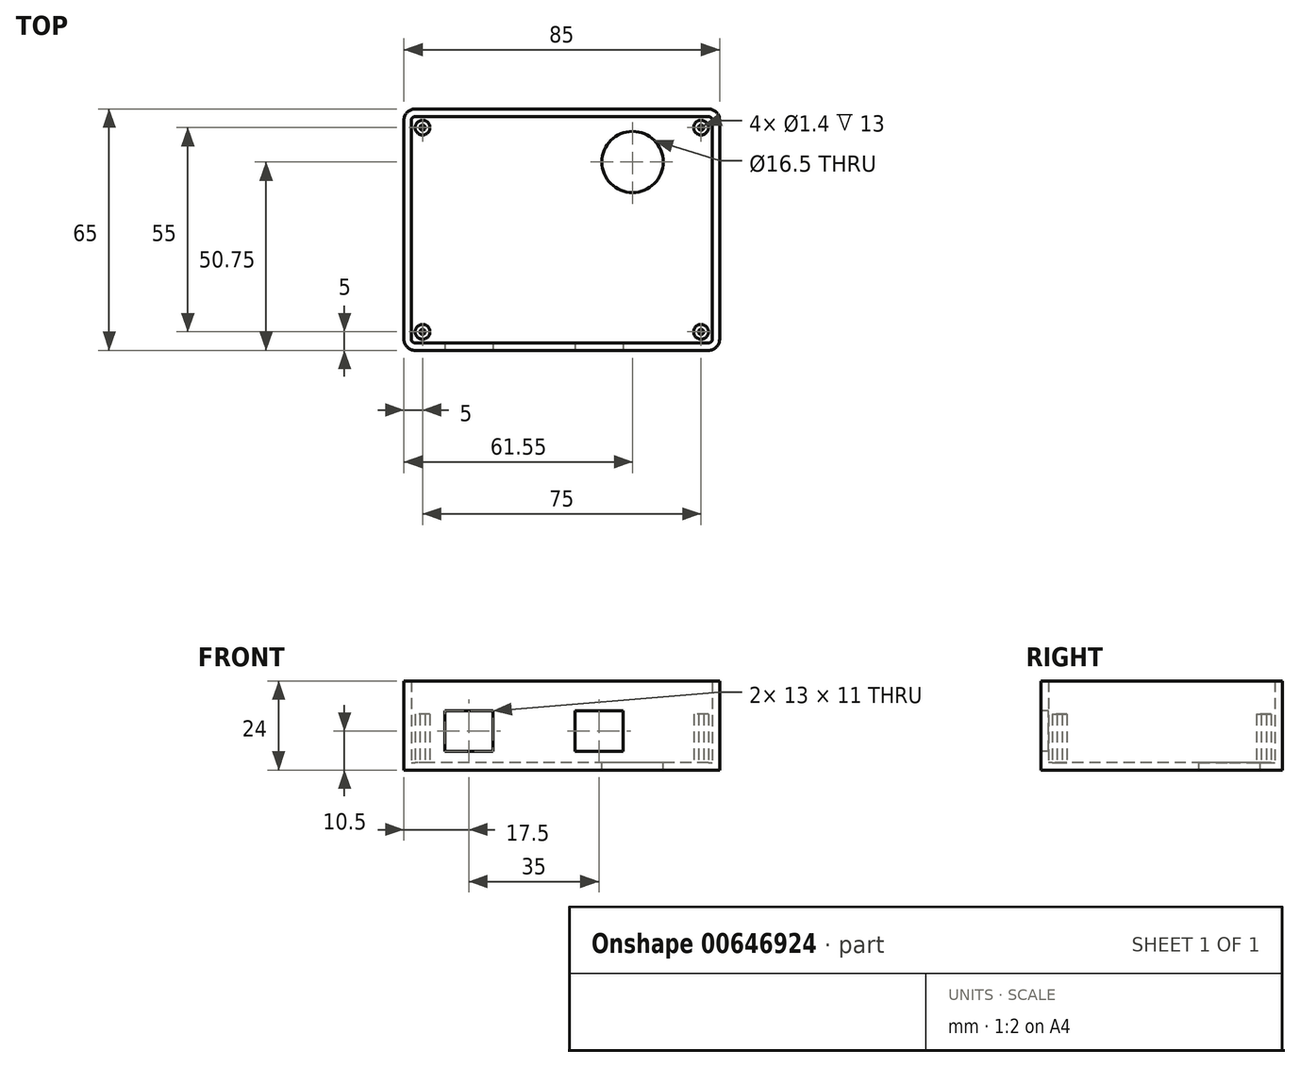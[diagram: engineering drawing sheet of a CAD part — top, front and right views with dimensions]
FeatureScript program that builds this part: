
annotation { "Feature Type Name" : "Feature", "Feature Type Description" : "" }
export const myFeature = defineFeature(function(context is Context, id is Id, definition is map)
    precondition{}
    {
        {
            var Q0;
            Q0=qCreatedBy(makeId("Top.planeOp"),FACE);
            var sketch = newSketch(context, id + "F0", { "sketchPlane" : qUnion([Q0])});
            skLineSegment(sketch, "E0.bottom", {"start": v(39.5, 32.5) * mm, "end": v(-39.5, 32.5) * mm});
            skLineSegment(sketch, "E0.top", {"start": v(39.5, -32.5) * mm, "end": v(-39.5, -32.5) * mm});
            skLineSegment(sketch, "E0.left", {"start": v(42.5, 29.5) * mm, "end": v(42.5, -29.5) * mm});
            skLineSegment(sketch, "E0.right", {"start": v(-42.5, 29.5) * mm, "end": v(-42.5, -29.5) * mm});
            skPoint(sketch, "E0.middle", {"position": v(0, 0) * mm});
            skPoint(sketch, "E1.visualSharp", {"position": v(-42.5, 32.5) * mm});
            skArc(sketch, "E1.filletArc", {"start": v(-39.5, 32.5) * mm, "mid": v(-41.62, 31.62) * mm, "end": v(-42.5, 29.5) * mm});
            skPoint(sketch, "E2.visualSharp", {"position": v(-42.5, -32.5) * mm});
            skArc(sketch, "E2.filletArc", {"start": v(-42.5, -29.5) * mm, "mid": v(-41.62, -31.62) * mm, "end": v(-39.5, -32.5) * mm});
            skPoint(sketch, "E3.visualSharp", {"position": v(42.5, -32.5) * mm});
            skArc(sketch, "E3.filletArc", {"start": v(39.5, -32.5) * mm, "mid": v(41.62, -31.62) * mm, "end": v(42.5, -29.5) * mm});
            skPoint(sketch, "E4.visualSharp", {"position": v(42.5, 32.5) * mm});
            skArc(sketch, "E4.filletArc", {"start": v(42.5, 29.5) * mm, "mid": v(41.62, 31.62) * mm, "end": v(39.5, 32.5) * mm});
            skSolve(sketch);
        }
        {
            var Q0;
            Q0=makeQuery(id+"F0.imprint","IMPRINT",FACE,{"disambiguationData":[TD([[makeQuery(id+"F0.imprint","IMPRINT",EDGE,{"derivedFrom":sQuery(id+"F0.wireOp",EDGE,"E0.bottom")}),1.0]])]});
            extrude(context, id + "F1", {"entities" : qUnion([Q0]), "depth" : 24 * mm, "offsetDistance" : 25 * mm});
        }
        {
            var Q0;
            Q0=makeQuery(id+"F1.opExtrude","CAP_FACE",FACE,{"disambiguationData":[OSD([sQuery(id+"F0.wireOp",EDGE,"E0.bottom"),sQuery(id+"F0.wireOp",EDGE,"E0.top"),sQuery(id+"F0.wireOp",EDGE,"E0.left"),sQuery(id+"F0.wireOp",EDGE,"E0.right"),sQuery(id+"F0.wireOp",EDGE,"E1.filletArc"),sQuery(id+"F0.wireOp",EDGE,"E2.filletArc"),sQuery(id+"F0.wireOp",EDGE,"E3.filletArc"),sQuery(id+"F0.wireOp",EDGE,"E4.filletArc")])],"isStart":false});
            shell(context, id + "F2", {"entities" : qUnion([Q0]), "thickness" : 2 * mm});
        }
        {
            var Q0;
            Q0=makeQuery(id+"F2.opShell","OFFSET_FACE",FACE,{"disambiguationData":[OSD([sQuery(id+"F0.wireOp",EDGE,"E0.bottom"),sQuery(id+"F0.wireOp",EDGE,"E0.top"),sQuery(id+"F0.wireOp",EDGE,"E0.left"),sQuery(id+"F0.wireOp",EDGE,"E0.right"),sQuery(id+"F0.wireOp",EDGE,"E1.filletArc"),sQuery(id+"F0.wireOp",EDGE,"E2.filletArc"),sQuery(id+"F0.wireOp",EDGE,"E3.filletArc"),sQuery(id+"F0.wireOp",EDGE,"E4.filletArc")])]});
            var sketch = newSketch(context, id + "F3", { "sketchPlane" : qUnion([Q0])});
            skCircle(sketch, "E5", {"center": v(19.05, 18.25) * mm, "radius": 8.25 * mm});
            skSolve(sketch);
        }
        {
            var Q0;
            Q0 = qSketchRegion(id + "F3", true);
            var Q1;
            Q1=makeQuery(id+"F1.opExtrude","CAP_FACE",FACE,{"disambiguationData":[OSD([sQuery(id+"F0.wireOp",EDGE,"E0.bottom"),sQuery(id+"F0.wireOp",EDGE,"E0.top"),sQuery(id+"F0.wireOp",EDGE,"E0.left"),sQuery(id+"F0.wireOp",EDGE,"E0.right"),sQuery(id+"F0.wireOp",EDGE,"E1.filletArc"),sQuery(id+"F0.wireOp",EDGE,"E2.filletArc"),sQuery(id+"F0.wireOp",EDGE,"E3.filletArc"),sQuery(id+"F0.wireOp",EDGE,"E4.filletArc")])],"isStart":true});
            extrude(context, id + "F4", {"entities" : qUnion([Q0]), "operationType" : NewBodyOperationType.REMOVE, "endBound" : BoundingType.UP_TO_SURFACE, "oppositeDirection" : true, "depth" : 25 * mm, "endBoundEntityFace" : qUnion([Q1]), "offsetDistance" : 25 * mm});
        }
        {
            var Q0;
            Q0=makeQuery(id+"F2.opShell","OFFSET_FACE",FACE,{"disambiguationData":[OSD([sQuery(id+"F0.wireOp",EDGE,"E0.bottom"),sQuery(id+"F0.wireOp",EDGE,"E0.top"),sQuery(id+"F0.wireOp",EDGE,"E0.left"),sQuery(id+"F0.wireOp",EDGE,"E0.right"),sQuery(id+"F0.wireOp",EDGE,"E1.filletArc"),sQuery(id+"F0.wireOp",EDGE,"E2.filletArc"),sQuery(id+"F0.wireOp",EDGE,"E3.filletArc"),sQuery(id+"F0.wireOp",EDGE,"E4.filletArc")])]});
            var sketch = newSketch(context, id + "F5", { "sketchPlane" : qUnion([Q0])});
            skCircle(sketch, "E6", {"center": v(-37.5, 27.5) * mm, "radius": 2 * mm});
            skCircle(sketch, "E7.MirrorC", {"center": v(37.5, 27.5) * mm, "radius": 2 * mm});
            skCircle(sketch, "E8.MirrorC", {"center": v(37.5, -27.5) * mm, "radius": 2 * mm});
            skCircle(sketch, "E9.MirrorC", {"center": v(-37.5, -27.5) * mm, "radius": 2 * mm});
            skCircle(sketch, "E10.0", {"center": v(-37.5, 27.5) * mm, "radius": 0.7 * mm});
            skCircle(sketch, "E11.MirrorC", {"center": v(37.5, 27.5) * mm, "radius": 0.7 * mm});
            skCircle(sketch, "E12.MirrorC", {"center": v(37.5, -27.5) * mm, "radius": 0.7 * mm});
            skCircle(sketch, "E13.MirrorC", {"center": v(-37.5, -27.5) * mm, "radius": 0.7 * mm});
            skSolve(sketch);
        }
        {
            var Q0;
            Q0 = qSketchRegion(id + "F5", true);
            extrude(context, id + "F6", {"entities" : qUnion([Q0]), "operationType" : NewBodyOperationType.ADD, "depth" : 13 * mm, "offsetDistance" : 25 * mm});
        }
        {
            var Q0;
            Q0=makeQuery(id+"F1.opExtrude","SWEPT_FACE",FACE,{"disambiguationData":[OSD([sQuery(id+"F0.wireOp",EDGE,"E0.top")])]});
            var sketch = newSketch(context, id + "F7", { "sketchPlane" : qUnion([Q0])});
            skLineSegment(sketch, "E14.bottom", {"start": v(16.5, 16) * mm, "end": v(3.5, 16) * mm});
            skLineSegment(sketch, "E14.top", {"start": v(16.5, 5) * mm, "end": v(3.5, 5) * mm});
            skLineSegment(sketch, "E14.left", {"start": v(16.5, 16) * mm, "end": v(16.5, 5) * mm});
            skLineSegment(sketch, "E14.right", {"start": v(3.5, 16) * mm, "end": v(3.5, 5) * mm});
            skLineSegment(sketch, "E15.bottom", {"start": v(-31.5, 16) * mm, "end": v(-18.5, 16) * mm});
            skLineSegment(sketch, "E15.top", {"start": v(-31.5, 5) * mm, "end": v(-18.5, 5) * mm});
            skLineSegment(sketch, "E15.left", {"start": v(-31.5, 16) * mm, "end": v(-31.5, 5) * mm});
            skLineSegment(sketch, "E15.right", {"start": v(-18.5, 16) * mm, "end": v(-18.5, 5) * mm});
            skSolve(sketch);
        }
        {
            var Q0;
            Q0 = qSketchRegion(id + "F7", true);
            var Q1;
            Q1=makeQuery(id+"F2.opShell","OFFSET_FACE",FACE,{"disambiguationData":[OSD([sQuery(id+"F0.wireOp",EDGE,"E0.top")])]});
            extrude(context, id + "F8", {"entities" : qUnion([Q0]), "operationType" : NewBodyOperationType.REMOVE, "endBound" : BoundingType.UP_TO_SURFACE, "oppositeDirection" : true, "depth" : 25 * mm, "endBoundEntityFace" : qUnion([Q1]), "offsetDistance" : 25 * mm});
        }
    });
